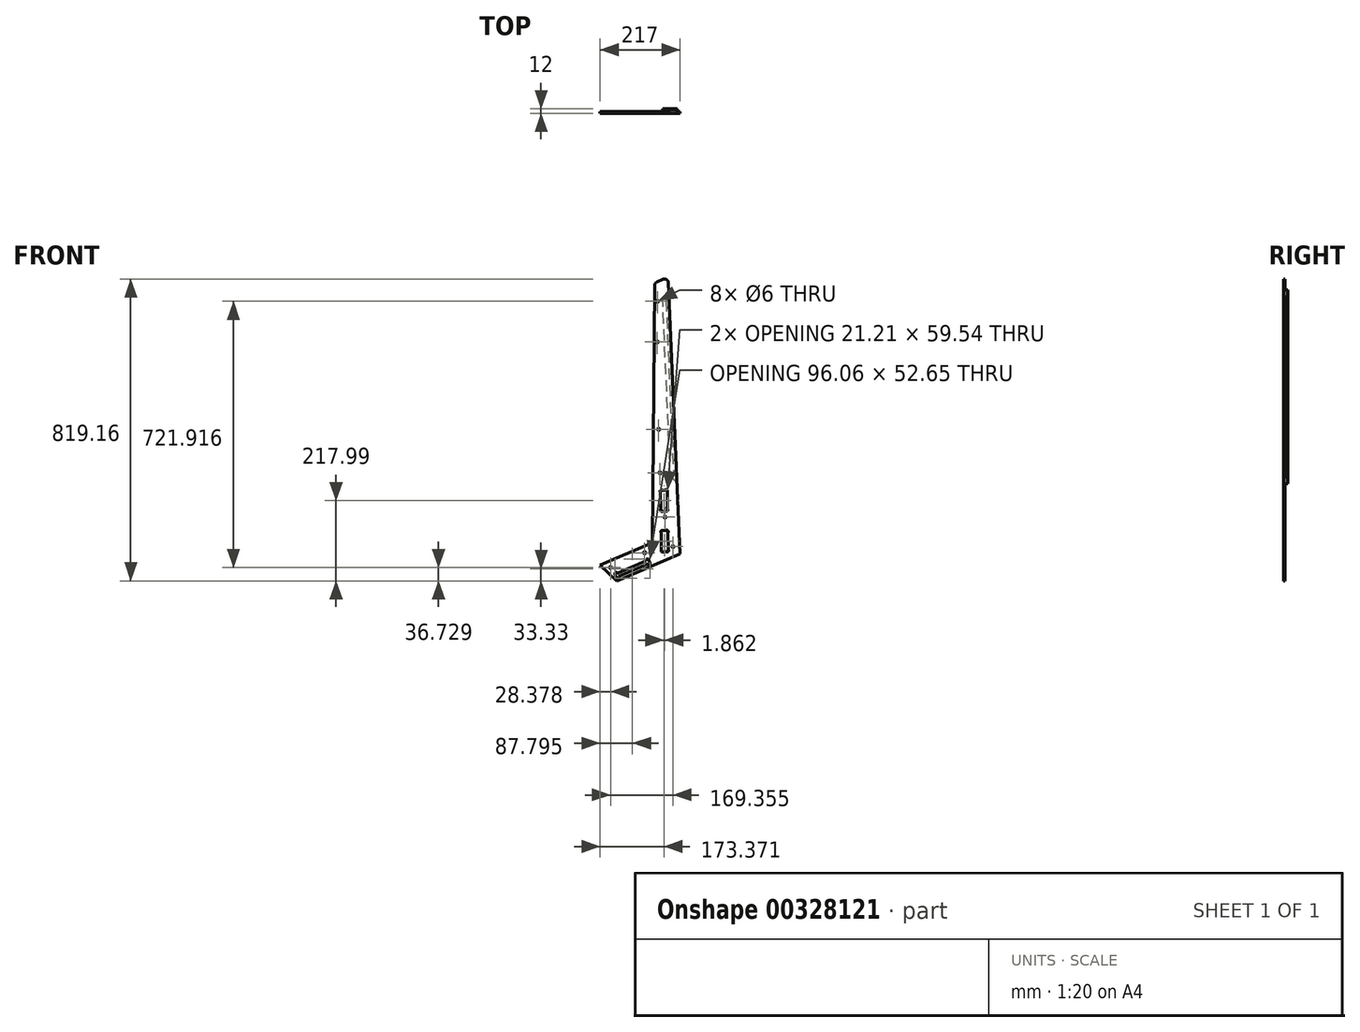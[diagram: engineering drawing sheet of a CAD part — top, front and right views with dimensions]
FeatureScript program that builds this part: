
annotation { "Feature Type Name" : "Feature", "Feature Type Description" : "" }
export const myFeature = defineFeature(function(context is Context, id is Id, definition is map)
    precondition{}
    {
        {
            var Q0;
            Q0=qCreatedBy(makeId("Front.planeOp"),FACE);
            var sketch = newSketch(context, id + "F0", { "sketchPlane" : qUnion([Q0])});
            skArc(sketch, "E0", {"start": v(65.23, -72.8) * mm, "mid": v(65.32, -78.46) * mm, "end": v(70.98, -78.36) * mm});
            skLineSegment(sketch, "E1", {"start": v(70.98, -78.36) * mm, "end": v(77.67, -78.25) * mm});
            skArc(sketch, "E2", {"start": v(77.67, -78.25) * mm, "mid": v(83.32, -78.15) * mm, "end": v(83.23, -72.5) * mm});
            skLineSegment(sketch, "E3", {"start": v(83.23, -72.5) * mm, "end": v(82.45, -26.82) * mm});
            skArc(sketch, "E4", {"start": v(82.45, -26.82) * mm, "mid": v(82.36, -21.16) * mm, "end": v(76.7, -21.26) * mm});
            skLineSegment(sketch, "E5", {"start": v(76.7, -21.26) * mm, "end": v(70.02, -21.37) * mm});
            skArc(sketch, "E6", {"start": v(70.02, -21.37) * mm, "mid": v(64.36, -21.47) * mm, "end": v(64.46, -27.12) * mm});
            skLineSegment(sketch, "E7", {"start": v(64.46, -27.12) * mm, "end": v(65.23, -72.8) * mm});
            skLineSegment(sketch, "E8", {"start": v(85.09, -182.48) * mm, "end": v(84.31, -136.8) * mm});
            skArc(sketch, "E9", {"start": v(84.31, -136.8) * mm, "mid": v(84.22, -131.15) * mm, "end": v(78.56, -131.24) * mm});
            skLineSegment(sketch, "E10", {"start": v(78.56, -131.24) * mm, "end": v(71.88, -131.35) * mm});
            skArc(sketch, "E11", {"start": v(71.88, -131.35) * mm, "mid": v(66.22, -131.45) * mm, "end": v(66.32, -137.1) * mm});
            skLineSegment(sketch, "E12", {"start": v(66.32, -137.1) * mm, "end": v(67.09, -182.79) * mm});
            skArc(sketch, "E13", {"start": v(67.09, -182.79) * mm, "mid": v(67.19, -188.44) * mm, "end": v(72.84, -188.35) * mm});
            skLineSegment(sketch, "E14", {"start": v(72.84, -188.35) * mm, "end": v(79.53, -188.23) * mm});
            skArc(sketch, "E15", {"start": v(79.53, -188.23) * mm, "mid": v(85.18, -188.14) * mm, "end": v(85.09, -182.48) * mm});
            skArc(sketch, "E16", {"start": v(-52.1, -246.94) * mm, "mid": v(-57.35, -244.85) * mm, "end": v(-59.44, -250.1) * mm});
            skLineSegment(sketch, "E17", {"start": v(-59.44, -250.1) * mm, "end": v(-55.88, -258.37) * mm});
            skArc(sketch, "E18", {"start": v(-55.88, -258.37) * mm, "mid": v(-50.62, -260.47) * mm, "end": v(-48.53, -255.21) * mm});
            skLineSegment(sketch, "E19", {"start": v(-48.53, -255.21) * mm, "end": v(28.62, -222) * mm});
            skArc(sketch, "E20", {"start": v(28.62, -222) * mm, "mid": v(33.88, -224.09) * mm, "end": v(35.97, -218.83) * mm});
            skLineSegment(sketch, "E21", {"start": v(35.97, -218.83) * mm, "end": v(32.41, -210.57) * mm});
            skArc(sketch, "E22", {"start": v(32.41, -210.57) * mm, "mid": v(27.15, -208.47) * mm, "end": v(25.06, -213.73) * mm});
            skLineSegment(sketch, "E23", {"start": v(25.06, -213.73) * mm, "end": v(-52.1, -246.94) * mm});
            skArc(sketch, "E24", {"start": v(41.94, -161.76) * mm, "mid": v(41.27, -163.94) * mm, "end": v(39.52, -165.4) * mm});
            skLineSegment(sketch, "E25", {"start": v(39.52, -165.4) * mm, "end": v(-99.53, -225.26) * mm});
            skLineSegment(sketch, "E26", {"start": v(-99.53, -225.26) * mm, "end": v(-53.74, -267.8) * mm});
            skLineSegment(sketch, "E27", {"start": v(-53.74, -267.8) * mm, "end": v(41.34, -226.86) * mm});
            skLineSegment(sketch, "E28", {"start": v(41.34, -226.86) * mm, "end": v(117.47, -194.09) * mm});
            skLineSegment(sketch, "E29", {"start": v(117.47, -194.09) * mm, "end": v(85.73, 541.79) * mm});
            skArc(sketch, "E30", {"start": v(85.73, 541.79) * mm, "mid": v(81.05, 549.82) * mm, "end": v(71.78, 550.54) * mm});
            skLineSegment(sketch, "E31", {"start": v(71.78, 550.54) * mm, "end": v(54.43, 543.07) * mm});
            skArc(sketch, "E32", {"start": v(54.43, 543.07) * mm, "mid": v(50.05, 539.42) * mm, "end": v(48.38, 533.98) * mm});
            skLineSegment(sketch, "E33", {"start": v(48.38, 533.98) * mm, "end": v(41.94, -161.76) * mm});
            skCircle(sketch, "E34", {"center": v(56.39, 490.84) * mm, "radius": 3 * mm});
            skCircle(sketch, "E35", {"center": v(55.37, 380.85) * mm, "radius": 3 * mm});
            skCircle(sketch, "E36", {"center": v(-71.15, -231.07) * mm, "radius": 3 * mm});
            skCircle(sketch, "E37", {"center": v(76.63, -94.57) * mm, "radius": 3 * mm});
            skCircle(sketch, "E38", {"center": v(21.3, -191.27) * mm, "radius": 3 * mm});
            skCircle(sketch, "E39", {"center": v(63.23, 25.56) * mm, "radius": 3 * mm});
            skCircle(sketch, "E40", {"center": v(59.35, 143.54) * mm, "radius": 3 * mm});
            skCircle(sketch, "E41", {"center": v(98.2, -174.5) * mm, "radius": 3 * mm});
            skLineSegment(sketch, "E42", {"start": v(96.02, 524.96) * mm, "end": v(118.95, -6.55) * mm});
            skArc(sketch, "E43", {"start": v(118.95, -6.55) * mm, "mid": v(114.38, -11.53) * mm, "end": v(109.4, -6.96) * mm});
            skLineSegment(sketch, "E44", {"start": v(109.4, -6.96) * mm, "end": v(109.28, -4.28) * mm});
            skArc(sketch, "E45", {"start": v(109.28, -4.28) * mm, "mid": v(108.54, -1.25) * mm, "end": v(106.7, 1.27) * mm});
            skLineSegment(sketch, "E46", {"start": v(106.7, 1.27) * mm, "end": v(92.42, 14.37) * mm});
            skArc(sketch, "E47", {"start": v(92.42, 14.37) * mm, "mid": v(91.5, 15.63) * mm, "end": v(91.13, 17.14) * mm});
            skLineSegment(sketch, "E48", {"start": v(91.13, 17.14) * mm, "end": v(70.34, 498.96) * mm});
            skArc(sketch, "E49", {"start": v(70.34, 498.96) * mm, "mid": v(70.58, 500.5) * mm, "end": v(71.4, 501.83) * mm});
            skLineSegment(sketch, "E50", {"start": v(71.4, 501.83) * mm, "end": v(84.49, 516.1) * mm});
            skArc(sketch, "E51", {"start": v(84.49, 516.1) * mm, "mid": v(86.11, 518.78) * mm, "end": v(86.59, 521.86) * mm});
            skLineSegment(sketch, "E52", {"start": v(86.59, 521.86) * mm, "end": v(86.47, 524.54) * mm});
            skArc(sketch, "E53", {"start": v(86.47, 524.54) * mm, "mid": v(91.04, 529.53) * mm, "end": v(96.02, 524.96) * mm});
            skArc(sketch, "E54", {"start": v(99.45, 23.9) * mm, "mid": v(99.82, 22.39) * mm, "end": v(100.74, 21.13) * mm});
            skLineSegment(sketch, "E55", {"start": v(100.74, 21.13) * mm, "end": v(106.05, 16.26) * mm});
            skArc(sketch, "E56", {"start": v(106.05, 16.26) * mm, "mid": v(107.9, 13.74) * mm, "end": v(108.63, 10.7) * mm});
            skLineSegment(sketch, "E57", {"start": v(108.63, 10.7) * mm, "end": v(108.75, 8.02) * mm});
            skArc(sketch, "E58", {"start": v(108.75, 8.02) * mm, "mid": v(113.73, 3.45) * mm, "end": v(118.3, 8.44) * mm});
            skArc(sketch, "E59", {"start": v(96.67, 509.97) * mm, "mid": v(91.69, 514.54) * mm, "end": v(87.12, 509.56) * mm});
            skLineSegment(sketch, "E60", {"start": v(87.12, 509.56) * mm, "end": v(87.23, 506.87) * mm});
            skArc(sketch, "E61", {"start": v(87.23, 506.87) * mm, "mid": v(86.76, 503.79) * mm, "end": v(85.14, 501.12) * mm});
            skLineSegment(sketch, "E62", {"start": v(85.14, 501.12) * mm, "end": v(80.27, 495.82) * mm});
            skArc(sketch, "E63", {"start": v(80.27, 495.82) * mm, "mid": v(79.46, 494.48) * mm, "end": v(79.22, 492.94) * mm});
            skLineSegment(sketch, "E64", {"start": v(79.22, 492.94) * mm, "end": v(99.45, 23.9) * mm});
            skSolve(sketch);
        }
        {
            var Q0;
            {var subQ3=sQuery(id+"F0.wireOp",EDGE,"E45");Q0=makeQuery(id+"F0.imprint","IMPRINT",FACE,{"disambiguationData":[TD([[makeQuery(id+"F0.imprint","IMPRINT",EDGE,{"derivedFrom":subQ3}),-1.0]])]});}
            var Q1;
            Q1=makeQuery(id+"F0.imprint","IMPRINT",FACE,{"disambiguationData":[TD([[makeQuery(id+"F0.imprint","IMPRINT",EDGE,{"derivedFrom":sQuery(id+"F0.wireOp",EDGE,"E54")}),1.0]])]});
            var Q2;
            Q2=makeQuery(id+"F0.imprint","IMPRINT",FACE,{"disambiguationData":[TD([[makeQuery(id+"F0.imprint","IMPRINT",EDGE,{"derivedFrom":sQuery(id+"F0.wireOp",EDGE,"E36")}),-1.0]])]});
            var Q3;
            Q3=makeQuery(id+"F0.imprint","IMPRINT",FACE,{"disambiguationData":[TD([[makeQuery(id+"F0.imprint","IMPRINT",EDGE,{"derivedFrom":sQuery(id+"F0.wireOp",EDGE,"E41")}),-1.0]])]});
            var Q4;
            Q4=makeQuery(id+"F0.imprint","IMPRINT",FACE,{"disambiguationData":[TD([[makeQuery(id+"F0.imprint","IMPRINT",EDGE,{"derivedFrom":sQuery(id+"F0.wireOp",EDGE,"E38")}),-1.0]])]});
            var Q5;
            Q5=makeQuery(id+"F0.imprint","IMPRINT",FACE,{"disambiguationData":[TD([[makeQuery(id+"F0.imprint","IMPRINT",EDGE,{"derivedFrom":sQuery(id+"F0.wireOp",EDGE,"E37")}),-1.0]])]});
            var Q6;
            Q6=makeQuery(id+"F0.imprint","IMPRINT",FACE,{"disambiguationData":[TD([[makeQuery(id+"F0.imprint","IMPRINT",EDGE,{"derivedFrom":sQuery(id+"F0.wireOp",EDGE,"E0")}),-1.0]])]});
            var Q7;
            Q7=makeQuery(id+"F0.imprint","IMPRINT",FACE,{"disambiguationData":[TD([[makeQuery(id+"F0.imprint","IMPRINT",EDGE,{"derivedFrom":sQuery(id+"F0.wireOp",EDGE,"E39")}),-1.0]])]});
            var Q8;
            Q8=makeQuery(id+"F0.imprint","IMPRINT",FACE,{"disambiguationData":[TD([[makeQuery(id+"F0.imprint","IMPRINT",EDGE,{"derivedFrom":sQuery(id+"F0.wireOp",EDGE,"E40")}),-1.0]])]});
            var Q9;
            Q9=makeQuery(id+"F0.imprint","IMPRINT",FACE,{"disambiguationData":[TD([[makeQuery(id+"F0.imprint","IMPRINT",EDGE,{"derivedFrom":sQuery(id+"F0.wireOp",EDGE,"E35")}),-1.0]])]});
            var Q10;
            Q10=makeQuery(id+"F0.imprint","IMPRINT",FACE,{"disambiguationData":[TD([[makeQuery(id+"F0.imprint","IMPRINT",EDGE,{"derivedFrom":sQuery(id+"F0.wireOp",EDGE,"E34")}),-1.0]])]});
            extrude(context, id + "F1", {"entities" : qUnion([Q0, Q1, Q2, Q3, Q4, Q5, Q6, Q7, Q8, Q9, Q10]), "depth" : 18 * mm});
        }
        {
            var Q0;
            Q0=makeQuery(id+"F0.imprint","IMPRINT",FACE,{"disambiguationData":[TD([[makeQuery(id+"F0.imprint","IMPRINT",EDGE,{"derivedFrom":sQuery(id+"F0.wireOp",EDGE,"E40")}),-1.0]])]});
            var Q1;
            Q1=makeQuery(id+"F0.imprint","IMPRINT",FACE,{"disambiguationData":[TD([[makeQuery(id+"F0.imprint","IMPRINT",EDGE,{"derivedFrom":sQuery(id+"F0.wireOp",EDGE,"E39")}),-1.0]])]});
            var Q2;
            Q2=makeQuery(id+"F0.imprint","IMPRINT",FACE,{"disambiguationData":[TD([[makeQuery(id+"F0.imprint","IMPRINT",EDGE,{"derivedFrom":sQuery(id+"F0.wireOp",EDGE,"E35")}),-1.0]])]});
            var Q3;
            Q3=makeQuery(id+"F0.imprint","IMPRINT",FACE,{"disambiguationData":[TD([[makeQuery(id+"F0.imprint","IMPRINT",EDGE,{"derivedFrom":sQuery(id+"F0.wireOp",EDGE,"E34")}),-1.0]])]});
            var Q4;
            Q4=makeQuery(id+"F0.imprint","IMPRINT",FACE,{"disambiguationData":[TD([[makeQuery(id+"F0.imprint","IMPRINT",EDGE,{"derivedFrom":sQuery(id+"F0.wireOp",EDGE,"E38")}),-1.0]])]});
            var Q5;
            Q5=makeQuery(id+"F0.imprint","IMPRINT",FACE,{"disambiguationData":[TD([[makeQuery(id+"F0.imprint","IMPRINT",EDGE,{"derivedFrom":sQuery(id+"F0.wireOp",EDGE,"E41")}),-1.0]])]});
            var Q6;
            Q6=makeQuery(id+"F0.imprint","IMPRINT",FACE,{"disambiguationData":[TD([[makeQuery(id+"F0.imprint","IMPRINT",EDGE,{"derivedFrom":sQuery(id+"F0.wireOp",EDGE,"E37")}),-1.0]])]});
            var Q7;
            Q7=makeQuery(id+"F0.imprint","IMPRINT",FACE,{"disambiguationData":[TD([[makeQuery(id+"F0.imprint","IMPRINT",EDGE,{"derivedFrom":sQuery(id+"F0.wireOp",EDGE,"E36")}),-1.0]])]});
            extrude(context, id + "F2", {"entities" : qUnion([Q0, Q1, Q2, Q3, Q4, Q5, Q6, Q7]), "operationType" : NewBodyOperationType.REMOVE, "depth" : 14 * mm});
        }
        {
            var Q0;
            Q0=makeQuery(id+"F0.imprint","IMPRINT",FACE,{"disambiguationData":[TD([[makeQuery(id+"F0.imprint","IMPRINT",EDGE,{"derivedFrom":sQuery(id+"F0.wireOp",EDGE,"E54")}),1.0]])]});
            extrude(context, id + "F3", {"entities" : qUnion([Q0]), "operationType" : NewBodyOperationType.REMOVE, "depth" : 9 * mm});
        }
        {
            var Q0;
            {var subQ3=sQuery(id+"F0.wireOp",EDGE,"E45");Q0=makeQuery(id+"F0.imprint","IMPRINT",FACE,{"disambiguationData":[TD([[makeQuery(id+"F0.imprint","IMPRINT",EDGE,{"derivedFrom":subQ3}),-1.0]])]});}
            extrude(context, id + "F4", {"entities" : qUnion([Q0]), "operationType" : NewBodyOperationType.REMOVE, "depth" : 6 * mm});
        }
    });
